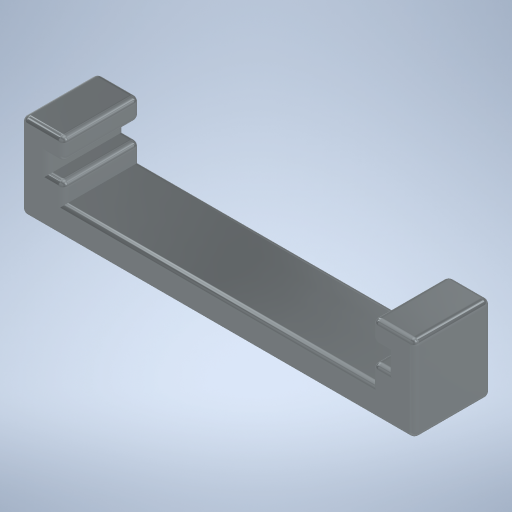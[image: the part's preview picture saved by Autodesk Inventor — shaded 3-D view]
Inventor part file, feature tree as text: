
AUTODESK INVENTOR PART (.ipt)
format: ipt  version: 2024.2 (Build 282272000, 272)  size: 355,840 bytes
history: native  units: mm
features: other x2, extrude x1, fillet x1, sketch x1
ambient origin geometry x8: Origin, YZ Plane, XZ Plane, XY Plane, X Axis, Y Axis, Z Axis, Center Point
bodies: Body1 (feature_tree)
feature tree (5):
  other  "Bryła1"
  extrude  "Wyciągnięcie proste1"  Depth=107.0mm
  fillet  "Zaokrąglenie1"  Radius=5.0mm
  sketch  "Szkic1"
  other  "Finish1"
